# Revit family: Toilet-Floor_Mount-KOHLER-Highline-K-26813
name_source: partatom
category: Plumbing Fixtures
units: mm (PartAtom-declared; Revit-internal decimal feet)

## family parameters
Cut with Voids When Loaded = No
Host = Face
OmniClass Number = 23.31.19.00
OmniClass Title = Toilets
Part Type = Normal
Room Calculation Point = No
Round Connector Dimension = Use Diameter
Shared = No

## types (2) — shared parameters
ADA Compliant = No
Assembly Code = D2010100
Bowl Height = 16 1/4"
CW Connection = Yes
Cold Water Inlet = Cold Water Inlet
Date Modified = 10/02/2024
Default Elevation = 0"
Description = One-piece elongated toilet, 1.28 gpf
Finish = Kohler-Vitreous_China-0-White
Flow Rate = 0 GPM
Flush Rate- GPF = 1.28 GPF
Flush Rate- LPF = 4.85 LPF
HW Connection = No
Height = 27 13/16"
Hot Water Inlet = Hot Water Inlet
Length = 28 11/16"
Manufacturer = Kohler Co.
Master Format 2014 = 22 42 13.13
Master Format 2014 Name = Residential Water Closets
Material = Vitreous China
Pressure = 0.00 psi
Product Documentation Link = https://www.us.kohler.com
Product Name = Highline
Product Page URL = http://www.us.kohler.com
Rough-In = 12"
Seat Included = Yes
URL = https://www.us.kohler.com
Vent Connection = No
Waste Connection = Yes
Waste Water Outlet = Waste Water Outlet
WaterSense Certified = No
Width = 17 11/16"

## per-type parameters (varying)
| type | Left Hand Trip Lever | Model | Right Hand Trip Lever | Type |
| Left Hand Trip Lever, 0-White | Yes | K-26813-0 | No | 1 |
| Right Hand Trip Lever, 0-White | No | K-26813-RA-0 | Yes | 2 |

## geometry (parser evidence)
native form markers: Sweep x7
no freeform markers — native parametric forms only
